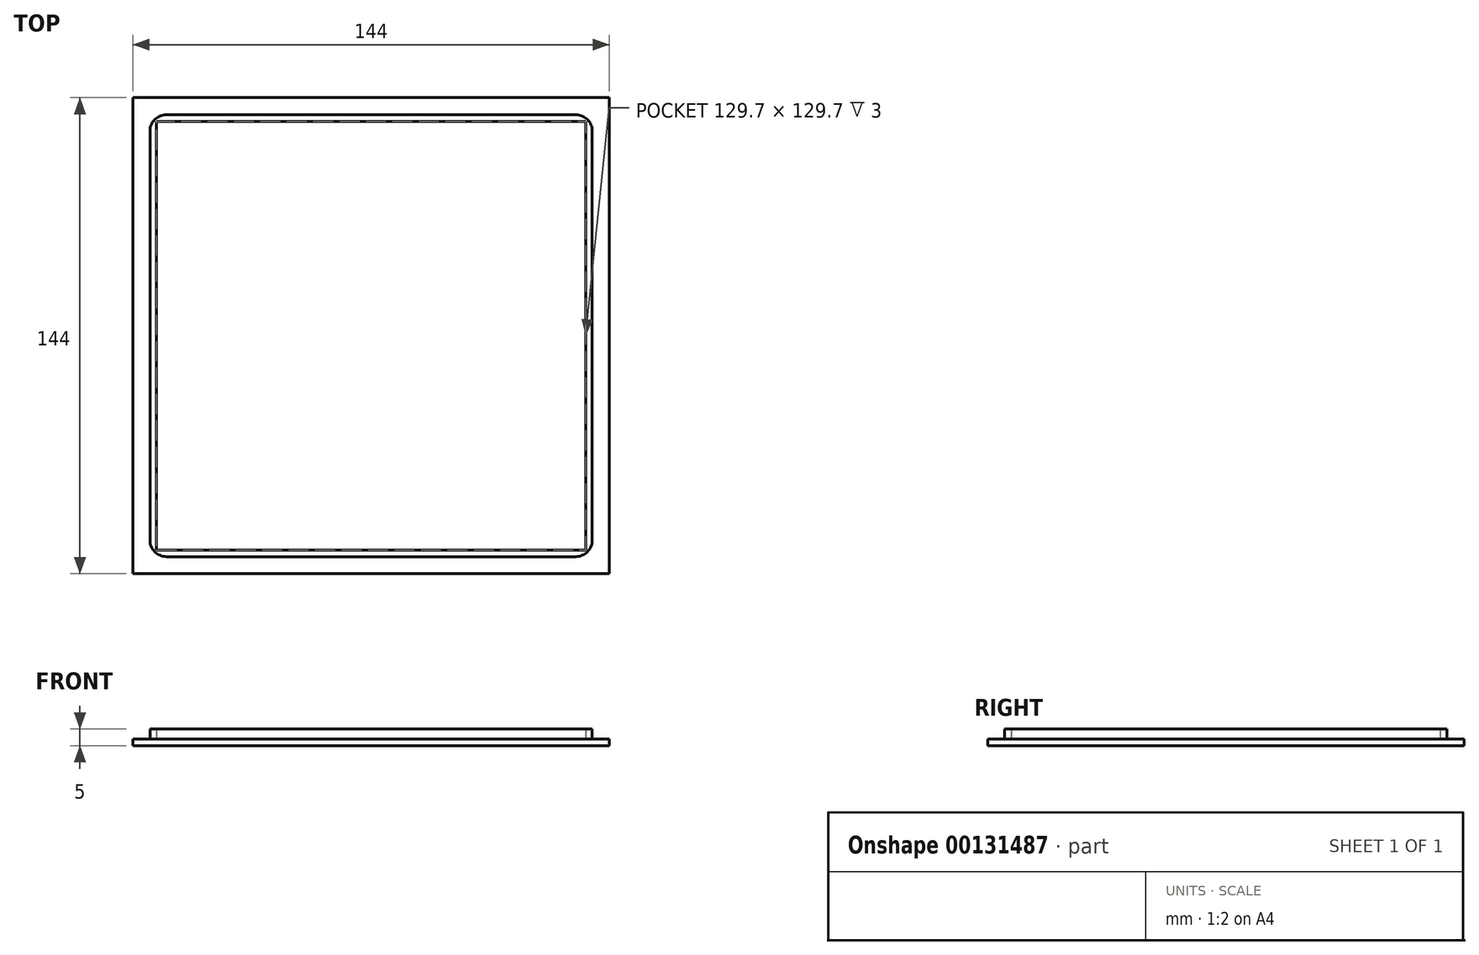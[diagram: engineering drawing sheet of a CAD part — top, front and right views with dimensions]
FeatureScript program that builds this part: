
annotation { "Feature Type Name" : "Feature", "Feature Type Description" : "" }
export const myFeature = defineFeature(function(context is Context, id is Id, definition is map)
    precondition{}
    {
        {
            var Q0;
            Q0=qCreatedBy(makeId("Top.planeOp"),FACE);
            var sketch = newSketch(context, id + "F0", { "sketchPlane" : qUnion([Q0])});
            skLineSegment(sketch, "E0.bottom", {"start": v(-46.91, 148.88) * mm, "end": v(97.09, 148.88) * mm});
            skLineSegment(sketch, "E0.top", {"start": v(-46.91, 4.88) * mm, "end": v(97.09, 4.88) * mm});
            skLineSegment(sketch, "E0.left", {"start": v(-46.91, 148.88) * mm, "end": v(-46.91, 4.88) * mm});
            skLineSegment(sketch, "E0.right", {"start": v(97.09, 148.88) * mm, "end": v(97.09, 4.88) * mm});
            skSolve(sketch);
        }
        {
            var Q0;
            Q0=makeQuery(id+"F0.imprint","IMPRINT",FACE,{"disambiguationData":[TD([[makeQuery(id+"F0.imprint","IMPRINT",EDGE,{"derivedFrom":sQuery(id+"F0.wireOp",EDGE,"E0.bottom")}),-1.0]])]});
            var sketch = newSketch(context, id + "F1", { "sketchPlane" : qUnion([Q0])});
            skLineSegment(sketch, "E1.0", {"start": v(-39.76, 141.73) * mm, "end": v(-39.76, 12.03) * mm});
            skLineSegment(sketch, "E1.1", {"start": v(-39.76, 141.73) * mm, "end": v(89.94, 141.73) * mm});
            skLineSegment(sketch, "E1.2", {"start": v(89.94, 141.73) * mm, "end": v(89.94, 12.03) * mm});
            skLineSegment(sketch, "E1.3", {"start": v(-39.76, 12.03) * mm, "end": v(89.94, 12.03) * mm});
            skLineSegment(sketch, "E2.0", {"start": v(91.94, 143.73) * mm, "end": v(-41.76, 143.73) * mm});
            skLineSegment(sketch, "E2.1", {"start": v(91.94, 10.03) * mm, "end": v(91.94, 143.73) * mm});
            skLineSegment(sketch, "E2.2", {"start": v(-41.76, 10.03) * mm, "end": v(91.94, 10.03) * mm});
            skLineSegment(sketch, "E2.3", {"start": v(-41.76, 143.73) * mm, "end": v(-41.76, 10.03) * mm});
            skSolve(sketch);
        }
        {
            var Q0;
            Q0=makeQuery(id+"F0.imprint","IMPRINT",FACE,{"disambiguationData":[TD([[makeQuery(id+"F0.imprint","IMPRINT",EDGE,{"derivedFrom":sQuery(id+"F0.wireOp",EDGE,"E0.bottom")}),-1.0]])]});
            extrude(context, id + "F2", {"entities" : qUnion([Q0]), "depth" : 2 * mm});
        }
        {
            var Q0;
            Q0=makeQuery(id+"F1.imprint","IMPRINT",FACE,{"disambiguationData":[TD([[makeQuery(id+"F1.imprint","IMPRINT",EDGE,{"derivedFrom":sQuery(id+"F1.wireOp",EDGE,"E1.0")}),-1.0]])]});
            extrude(context, id + "F3", {"entities" : qUnion([Q0]), "operationType" : NewBodyOperationType.ADD, "depth" : 5 * mm});
        }
        {
            var Q0;
            Q0=makeQuery(id+"F3.opExtrude","SWEPT_EDGE",EDGE,{"disambiguationData":[OSD([sQuery(id+"F1.wireOp",EDGE,"E2.0"),sQuery(id+"F1.wireOp",EDGE,"E2.3")])]});
            var Q1;
            Q1=makeQuery(id+"F3.opExtrude","SWEPT_EDGE",EDGE,{"disambiguationData":[OSD([sQuery(id+"F1.wireOp",EDGE,"E2.0"),sQuery(id+"F1.wireOp",EDGE,"E2.1")])]});
            var Q2;
            Q2=makeQuery(id+"F3.opExtrude","SWEPT_EDGE",EDGE,{"disambiguationData":[OSD([sQuery(id+"F1.wireOp",EDGE,"E2.2"),sQuery(id+"F1.wireOp",EDGE,"E2.3")])]});
            var Q3;
            Q3=makeQuery(id+"F3.opExtrude","SWEPT_EDGE",EDGE,{"disambiguationData":[OSD([sQuery(id+"F1.wireOp",EDGE,"E2.1"),sQuery(id+"F1.wireOp",EDGE,"E2.2")])]});
            fillet(context, id + "F4", {"entities" : qUnion([Q0, Q1, Q2, Q3]), "radius" : 5 * mm, "tangentPropagation" : true, "allowEdgeOverflow" : false});
        }
    });
